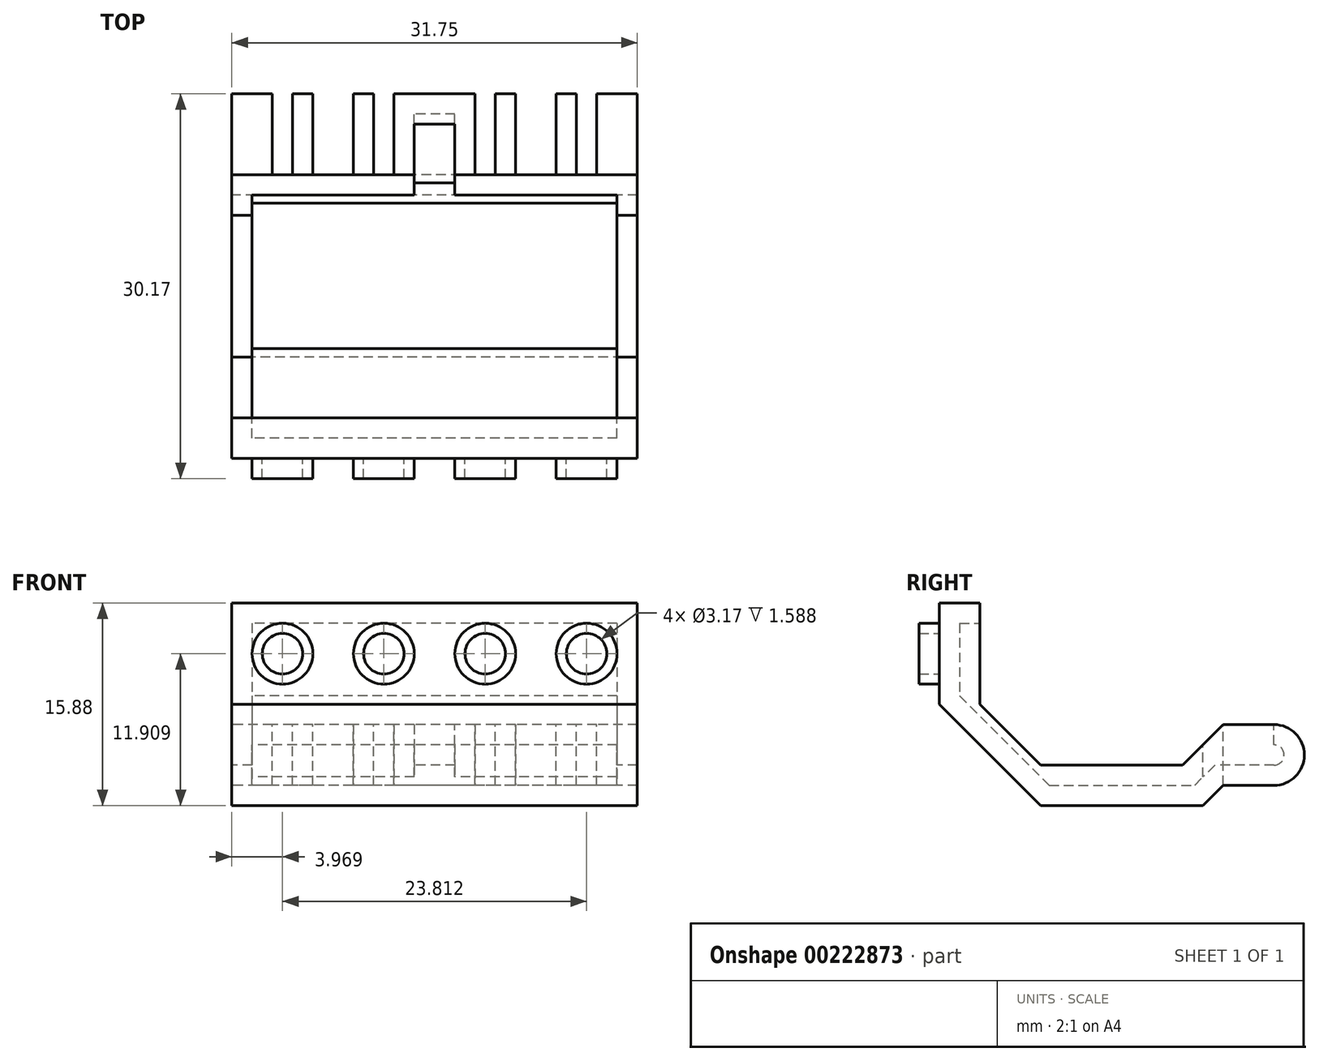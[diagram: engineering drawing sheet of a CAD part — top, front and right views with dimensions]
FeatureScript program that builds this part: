
annotation { "Feature Type Name" : "Feature", "Feature Type Description" : "" }
export const myFeature = defineFeature(function(context is Context, id is Id, definition is map)
    precondition{}
    {
        {
            var Q0;
            Q0=qCreatedBy(makeId("Right.planeOp"),FACE);
            var sketch = newSketch(context, id + "F0", { "sketchPlane" : qUnion([Q0])});
            skLineSegment(sketch, "E0.bottom", {"start": v(-14.29, 7.94) * mm, "end": v(14.29, 7.94) * mm});
            skLineSegment(sketch, "E0.top", {"start": v(-14.29, -7.94) * mm, "end": v(14.29, -7.94) * mm});
            skLineSegment(sketch, "E0.left", {"start": v(-14.29, 7.94) * mm, "end": v(-14.29, -7.94) * mm});
            skLineSegment(sketch, "E0.right", {"start": v(14.29, 7.94) * mm, "end": v(14.29, -7.94) * mm});
            skPoint(sketch, "E0.middle", {"position": v(0, 0) * mm});
            skPoint(sketch, "E1", {"position": v(-11.11, 7.94) * mm});
            skPoint(sketch, "E2", {"position": v(-14.29, 0) * mm});
            skLineSegment(sketch, "E3", {"start": v(-14.29, 0) * mm, "end": v(-6.35, -7.94) * mm});
            skLineSegment(sketch, "E4", {"start": v(-11.11, 7.94) * mm, "end": v(-11.11, 0) * mm});
            skPoint(sketch, "E5", {"position": v(6.35, -7.94) * mm});
            skLineSegment(sketch, "E6", {"start": v(-11.11, 0) * mm, "end": v(-6.35, -4.76) * mm});
            skPoint(sketch, "E7", {"position": v(4.76, -4.76) * mm});
            skLineSegment(sketch, "E8", {"start": v(-6.35, -4.76) * mm, "end": v(4.76, -4.76) * mm});
            skLineSegment(sketch, "E9", {"start": v(4.76, -4.76) * mm, "end": v(14.29, 4.76) * mm});
            skPoint(sketch, "E10", {"position": v(7.94, -6.35) * mm});
            skPoint(sketch, "E11", {"position": v(7.94, -1.59) * mm});
            skLineSegment(sketch, "E12", {"start": v(7.94, -6.35) * mm, "end": v(14.29, -6.35) * mm});
            skLineSegment(sketch, "E13", {"start": v(6.35, -7.94) * mm, "end": v(7.94, -6.35) * mm});
            skLineSegment(sketch, "E14", {"start": v(7.94, -1.59) * mm, "end": v(14.29, -1.59) * mm});
            skLineSegment(sketch, "E15", {"start": v(7.94, -1.59) * mm, "end": v(7.94, -6.35) * mm});
            skLineSegment(sketch, "E16", {"start": v(-6.35, -4.76) * mm, "end": v(-6.35, -7.94) * mm});
            skPoint(sketch, "E17", {"position": v(14.29, -3.97) * mm});
            skLineSegment(sketch, "E18", {"start": v(14.29, -3.97) * mm, "end": v(11.9, -3.97) * mm});
            skCircle(sketch, "E19", {"center": v(11.9, -3.97) * mm, "radius": 2.38 * mm});
            skSolve(sketch);
        }
        {
            var Q0;
            {var subQ1=sQuery(id+"F0.wireOp",EDGE,"E3");Q0=makeQuery(id+"F0.imprint","IMPRINT",FACE,{"disambiguationData":[TD([[makeQuery(id+"F0.imprint","IMPRINT",EDGE,{"derivedFrom":subQ1}),1.0]])]});}
            var Q1;
            {var subQ1=sQuery(id+"F0.wireOp",EDGE,"E8");Q1=makeQuery(id+"F0.imprint","IMPRINT",FACE,{"disambiguationData":[TD([[makeQuery(id+"F0.imprint","IMPRINT",EDGE,{"derivedFrom":subQ1}),-1.0]])]});}
            var Q2;
            {var subQ0=sQuery(id+"F0.wireOp",EDGE,"E15");Q2=makeQuery(id+"F0.imprint","IMPRINT",FACE,{"disambiguationData":[TD([[makeQuery(id+"F0.imprint","IMPRINT",EDGE,{"derivedFrom":subQ0}),1.0]])]});}
            var Q3;
            {var subQ0=sQuery(id+"F0.wireOp",EDGE,"E19");var subQ1=makeQuery(id+"F0.imprint","INTERSECT",VERTEX,{"derivedFrom":[sQuery(id+"F0.wireOp",EDGE,"E0.right"),subQ0]});Q3=makeQuery(id+"F0.imprint","IMPRINT",FACE,{"disambiguationData":[TD([[makeQuery(id+"F0.imprint","IMPRINT",EDGE,{"disambiguationData":[TD([[subQ1,-1.0]])],"derivedFrom":subQ0}),1.0]])]});}
            extrude(context, id + "F1", {"entities" : qUnion([Q0, Q1, Q2, Q3]), "depth" : 31.75 * mm});
        }
        {
            var Q0;
            Q0=makeQuery(id+"F1.opExtrude","SWEPT_FACE",FACE,{"disambiguationData":[OSD([sQuery(id+"F0.wireOp",EDGE,"E0.left")])]});
            var sketch = newSketch(context, id + "F2", { "sketchPlane" : qUnion([Q0])});
            skCircle(sketch, "E20", {"center": v(3.97, 3.97) * mm, "radius": 2.38 * mm});
            skCircle(sketch, "E21.0", {"center": v(3.97, 3.97) * mm, "radius": 1.59 * mm});
            skCircle(sketch, "E22.1.0.0", {"center": v(11.9, 3.97) * mm, "radius": 2.38 * mm});
            skCircle(sketch, "E22.1.0.1", {"center": v(11.9, 3.97) * mm, "radius": 1.59 * mm});
            skCircle(sketch, "E22.2.0.0", {"center": v(19.84, 3.97) * mm, "radius": 2.38 * mm});
            skCircle(sketch, "E22.2.0.1", {"center": v(19.84, 3.97) * mm, "radius": 1.59 * mm});
            skCircle(sketch, "E22.3.0.0", {"center": v(27.78, 3.97) * mm, "radius": 2.38 * mm});
            skCircle(sketch, "E22.3.0.1", {"center": v(27.78, 3.97) * mm, "radius": 1.59 * mm});
            skLineSegment(sketch, "E22.direction1", {"start": v(3.97, 3.97) * mm, "end": v(11.9, 3.97) * mm, "construction": true});
            skSolve(sketch);
        }
        {
            var Q0;
            Q0 = qSketchRegion(id + "F2", true);
            extrude(context, id + "F3", {"entities" : qUnion([Q0]), "operationType" : NewBodyOperationType.ADD, "depth" : 1.59 * mm});
        }
        {
            var Q0;
            Q0=makeQuery(id+"F1.opExtrude","SWEPT_FACE",FACE,{"disambiguationData":[OSD([sQuery(id+"F0.wireOp",EDGE,"E14")])]});
            var sketch = newSketch(context, id + "F4", { "sketchPlane" : qUnion([Q0])});
            skPoint(sketch, "E23", {"position": v(3.18, 7.94) * mm});
            skPoint(sketch, "E24", {"position": v(4.76, 7.94) * mm});
            skPoint(sketch, "E25", {"position": v(6.35, 7.94) * mm});
            skPoint(sketch, "E26", {"position": v(9.53, 7.94) * mm});
            skPoint(sketch, "E27", {"position": v(11.11, 7.94) * mm});
            skPoint(sketch, "E28", {"position": v(12.7, 7.94) * mm});
            skPoint(sketch, "E29.MirrorP", {"position": v(19.05, 7.94) * mm});
            skPoint(sketch, "E30.MirrorP", {"position": v(20.64, 7.94) * mm});
            skPoint(sketch, "E31.MirrorP", {"position": v(22.23, 7.94) * mm});
            skPoint(sketch, "E32.MirrorP", {"position": v(25.4, 7.94) * mm});
            skPoint(sketch, "E33.MirrorP", {"position": v(26.99, 7.94) * mm});
            skPoint(sketch, "E34.MirrorP", {"position": v(28.57, 7.94) * mm});
            skLineSegment(sketch, "E35", {"start": v(3.18, 7.94) * mm, "end": v(3.18, 14.29) * mm});
            skLineSegment(sketch, "E36", {"start": v(4.76, 7.94) * mm, "end": v(4.76, 14.29) * mm});
            skLineSegment(sketch, "E37", {"start": v(3.18, 14.29) * mm, "end": v(4.76, 14.29) * mm});
            skLineSegment(sketch, "E38", {"start": v(6.35, 7.94) * mm, "end": v(6.35, 14.29) * mm});
            skLineSegment(sketch, "E39", {"start": v(6.35, 14.29) * mm, "end": v(9.53, 14.29) * mm});
            skLineSegment(sketch, "E40", {"start": v(9.53, 14.29) * mm, "end": v(9.53, 7.94) * mm});
            skLineSegment(sketch, "E41", {"start": v(11.11, 7.94) * mm, "end": v(11.11, 14.29) * mm});
            skLineSegment(sketch, "E42", {"start": v(11.11, 14.29) * mm, "end": v(12.7, 14.29) * mm});
            skLineSegment(sketch, "E43", {"start": v(12.7, 14.29) * mm, "end": v(12.7, 7.94) * mm});
            skLineSegment(sketch, "E44.MirrorCS", {"start": v(19.05, 14.29) * mm, "end": v(19.05, 7.94) * mm});
            skLineSegment(sketch, "E45.MirrorCS", {"start": v(20.64, 7.94) * mm, "end": v(20.64, 14.29) * mm});
            skLineSegment(sketch, "E46.MirrorCS", {"start": v(20.64, 14.29) * mm, "end": v(19.05, 14.29) * mm});
            skLineSegment(sketch, "E47.MirrorCS", {"start": v(22.23, 14.29) * mm, "end": v(22.23, 7.94) * mm});
            skLineSegment(sketch, "E48.MirrorCS", {"start": v(25.4, 14.29) * mm, "end": v(22.23, 14.29) * mm});
            skLineSegment(sketch, "E49.MirrorCS", {"start": v(25.4, 7.94) * mm, "end": v(25.4, 14.29) * mm});
            skLineSegment(sketch, "E50.MirrorCS", {"start": v(26.99, 7.94) * mm, "end": v(26.99, 14.29) * mm});
            skLineSegment(sketch, "E51.MirrorCS", {"start": v(28.57, 14.29) * mm, "end": v(26.99, 14.29) * mm});
            skLineSegment(sketch, "E52.MirrorCS", {"start": v(28.57, 7.94) * mm, "end": v(28.57, 14.29) * mm});
            skSolve(sketch);
        }
        {
            var Q0;
            {var subQ0=sQuery(id+"F4.wireOp",EDGE,"E37");Q0=makeQuery(id+"F4.imprint","IMPRINT",FACE,{"disambiguationData":[TD([[makeQuery(id+"F4.imprint","IMPRINT",EDGE,{"derivedFrom":subQ0}),-1.0]])]});}
            var Q1;
            {var subQ0=sQuery(id+"F4.wireOp",EDGE,"E35");var subQ1=sQuery(id+"F0.wireOp",EDGE,"E14");var subQ4=makeQuery(id+"F1.opExtrude","SWEPT_EDGE",EDGE,{"disambiguationData":[OSD([subQ1,sQuery(id+"F0.wireOp",EDGE,"E19")])]});var subQ5=makeQuery(id+"F4.imprint","INTERSECT",VERTEX,{"derivedFrom":[subQ4,subQ0]});Q1=makeQuery(id+"F4.imprint","IMPRINT",FACE,{"disambiguationData":[TD([[makeQuery(id+"F4.imprint","IMPRINT",EDGE,{"disambiguationData":[TD([[subQ5,1.0]])],"derivedFrom":subQ0}),-1.0]])]});}
            var Q2;
            {var subQ0=sQuery(id+"F4.wireOp",EDGE,"E38");var subQ1=sQuery(id+"F0.wireOp",EDGE,"E14");var subQ4=makeQuery(id+"F1.opExtrude","SWEPT_EDGE",EDGE,{"disambiguationData":[OSD([subQ1,sQuery(id+"F0.wireOp",EDGE,"E19")])]});var subQ5=makeQuery(id+"F4.imprint","INTERSECT",VERTEX,{"derivedFrom":[subQ4,subQ0]});Q2=makeQuery(id+"F4.imprint","IMPRINT",FACE,{"disambiguationData":[TD([[makeQuery(id+"F4.imprint","IMPRINT",EDGE,{"disambiguationData":[TD([[subQ5,1.0]])],"derivedFrom":subQ0}),-1.0]])]});}
            var Q3;
            {var subQ0=sQuery(id+"F4.wireOp",EDGE,"E39");Q3=makeQuery(id+"F4.imprint","IMPRINT",FACE,{"disambiguationData":[TD([[makeQuery(id+"F4.imprint","IMPRINT",EDGE,{"derivedFrom":subQ0}),-1.0]])]});}
            var Q4;
            {var subQ0=sQuery(id+"F4.wireOp",EDGE,"E42");Q4=makeQuery(id+"F4.imprint","IMPRINT",FACE,{"disambiguationData":[TD([[makeQuery(id+"F4.imprint","IMPRINT",EDGE,{"derivedFrom":subQ0}),-1.0]])]});}
            var Q5;
            {var subQ0=sQuery(id+"F4.wireOp",EDGE,"E41");var subQ1=sQuery(id+"F0.wireOp",EDGE,"E14");var subQ4=makeQuery(id+"F1.opExtrude","SWEPT_EDGE",EDGE,{"disambiguationData":[OSD([subQ1,sQuery(id+"F0.wireOp",EDGE,"E19")])]});var subQ5=makeQuery(id+"F4.imprint","INTERSECT",VERTEX,{"derivedFrom":[subQ4,subQ0]});Q5=makeQuery(id+"F4.imprint","IMPRINT",FACE,{"disambiguationData":[TD([[makeQuery(id+"F4.imprint","IMPRINT",EDGE,{"disambiguationData":[TD([[subQ5,1.0]])],"derivedFrom":subQ0}),-1.0]])]});}
            var Q6;
            {var subQ0=sQuery(id+"F4.wireOp",EDGE,"E44.MirrorCS");var subQ1=sQuery(id+"F0.wireOp",EDGE,"E14");var subQ4=makeQuery(id+"F1.opExtrude","SWEPT_EDGE",EDGE,{"disambiguationData":[OSD([subQ1,sQuery(id+"F0.wireOp",EDGE,"E19")])]});var subQ5=makeQuery(id+"F4.imprint","INTERSECT",VERTEX,{"derivedFrom":[subQ4,subQ0]});Q6=makeQuery(id+"F4.imprint","IMPRINT",FACE,{"disambiguationData":[TD([[makeQuery(id+"F4.imprint","IMPRINT",EDGE,{"disambiguationData":[TD([[subQ5,-1.0]])],"derivedFrom":subQ0}),1.0]])]});}
            var Q7;
            {var subQ0=sQuery(id+"F4.wireOp",EDGE,"E46.MirrorCS");Q7=makeQuery(id+"F4.imprint","IMPRINT",FACE,{"disambiguationData":[TD([[makeQuery(id+"F4.imprint","IMPRINT",EDGE,{"derivedFrom":subQ0}),1.0]])]});}
            var Q8;
            {var subQ0=sQuery(id+"F4.wireOp",EDGE,"E48.MirrorCS");Q8=makeQuery(id+"F4.imprint","IMPRINT",FACE,{"disambiguationData":[TD([[makeQuery(id+"F4.imprint","IMPRINT",EDGE,{"derivedFrom":subQ0}),1.0]])]});}
            var Q9;
            {var subQ0=sQuery(id+"F4.wireOp",EDGE,"E47.MirrorCS");var subQ1=sQuery(id+"F0.wireOp",EDGE,"E14");var subQ4=makeQuery(id+"F1.opExtrude","SWEPT_EDGE",EDGE,{"disambiguationData":[OSD([subQ1,sQuery(id+"F0.wireOp",EDGE,"E19")])]});var subQ5=makeQuery(id+"F4.imprint","INTERSECT",VERTEX,{"derivedFrom":[subQ4,subQ0]});Q9=makeQuery(id+"F4.imprint","IMPRINT",FACE,{"disambiguationData":[TD([[makeQuery(id+"F4.imprint","IMPRINT",EDGE,{"disambiguationData":[TD([[subQ5,-1.0]])],"derivedFrom":subQ0}),1.0]])]});}
            var Q10;
            {var subQ0=sQuery(id+"F4.wireOp",EDGE,"E50.MirrorCS");var subQ1=sQuery(id+"F0.wireOp",EDGE,"E14");var subQ4=makeQuery(id+"F1.opExtrude","SWEPT_EDGE",EDGE,{"disambiguationData":[OSD([subQ1,sQuery(id+"F0.wireOp",EDGE,"E19")])]});var subQ5=makeQuery(id+"F4.imprint","INTERSECT",VERTEX,{"derivedFrom":[subQ4,subQ0]});Q10=makeQuery(id+"F4.imprint","IMPRINT",FACE,{"disambiguationData":[TD([[makeQuery(id+"F4.imprint","IMPRINT",EDGE,{"disambiguationData":[TD([[subQ5,1.0]])],"derivedFrom":subQ0}),-1.0]])]});}
            var Q11;
            {var subQ0=sQuery(id+"F4.wireOp",EDGE,"E51.MirrorCS");Q11=makeQuery(id+"F4.imprint","IMPRINT",FACE,{"disambiguationData":[TD([[makeQuery(id+"F4.imprint","IMPRINT",EDGE,{"derivedFrom":subQ0}),1.0]])]});}
            extrude(context, id + "F5", {"entities" : qUnion([Q0, Q1, Q2, Q3, Q4, Q5, Q6, Q7, Q8, Q9, Q10, Q11]), "operationType" : NewBodyOperationType.REMOVE, "oppositeDirection" : true, "depth" : 25.4 * mm});
        }
        {
            var Q0;
            {var subQ0=sQuery(id+"F4.wireOp",EDGE,"E35");var subQ3=sQuery(id+"F0.wireOp",EDGE,"E14");Q0=makeQuery(id+"F5.boolean.opBoolean","SPLIT",FACE,{"disambiguationData":[TD([makeQuery(id+"F5.opExtrude","SWEPT_FACE",FACE,{"disambiguationData":[OSD([subQ0])]})])],"derivedFrom":makeQuery(id+"F1.opExtrude","SWEPT_FACE",FACE,{"disambiguationData":[OSD([subQ3])]})});}
            var Q1;
            Q1=makeQuery(id+"F1.opExtrude","SWEPT_FACE",FACE,{"disambiguationData":[OSD([sQuery(id+"F0.wireOp",EDGE,"E9")])]});
            var Q2;
            {var subQ1=sQuery(id+"F4.wireOp",EDGE,"E43");var subQ4=sQuery(id+"F0.wireOp",EDGE,"E14");Q2=makeQuery(id+"F5.boolean.opBoolean","SPLIT",FACE,{"disambiguationData":[TD([makeQuery(id+"F5.opExtrude","SWEPT_FACE",FACE,{"disambiguationData":[OSD([subQ1])]})])],"derivedFrom":makeQuery(id+"F1.opExtrude","SWEPT_FACE",FACE,{"disambiguationData":[OSD([subQ4])]})});}
            var Q3;
            {var subQ1=sQuery(id+"F0.wireOp",EDGE,"E14");var subQ3=sQuery(id+"F4.wireOp",EDGE,"E52.MirrorCS");Q3=makeQuery(id+"F5.boolean.opBoolean","SPLIT",FACE,{"disambiguationData":[TD([makeQuery(id+"F5.opExtrude","SWEPT_FACE",FACE,{"disambiguationData":[OSD([subQ3])]})])],"derivedFrom":makeQuery(id+"F1.opExtrude","SWEPT_FACE",FACE,{"disambiguationData":[OSD([subQ1])]})});}
            var Q4;
            Q4=makeQuery(id+"F1.opExtrude","SWEPT_FACE",FACE,{"disambiguationData":[OSD([sQuery(id+"F0.wireOp",EDGE,"E8")])]});
            var Q5;
            Q5=makeQuery(id+"F1.opExtrude","SWEPT_FACE",FACE,{"disambiguationData":[OSD([sQuery(id+"F0.wireOp",EDGE,"E6")])]});
            var Q6;
            Q6=makeQuery(id+"F1.opExtrude","SWEPT_FACE",FACE,{"disambiguationData":[OSD([sQuery(id+"F0.wireOp",EDGE,"E4")])]});
            shell(context, id + "F6", {"entities" : qUnion([Q0, Q1, Q2, Q3, Q4, Q5, Q6]), "thickness" : 1.59 * mm});
        }
    });
